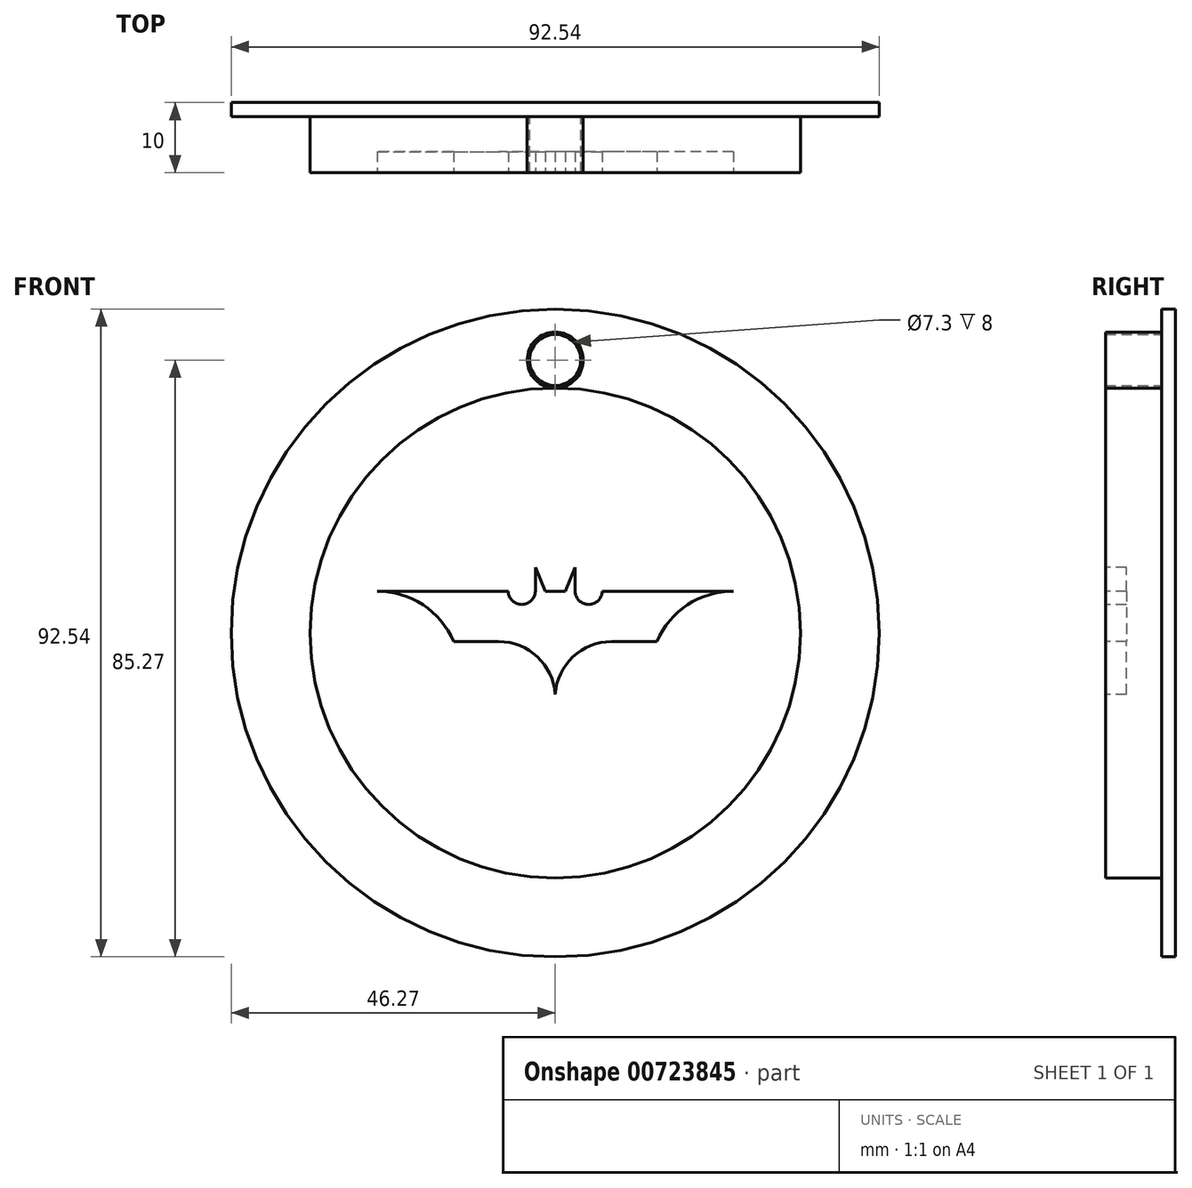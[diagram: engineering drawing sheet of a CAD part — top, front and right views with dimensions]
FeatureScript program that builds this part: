
annotation { "Feature Type Name" : "Feature", "Feature Type Description" : "" }
export const myFeature = defineFeature(function(context is Context, id is Id, definition is map)
    precondition{}
    {
        {
            var Q0;
            Q0=qCreatedBy(makeId("Front.planeOp"),FACE);
            var sketch = newSketch(context, id + "F0", { "sketchPlane" : qUnion([Q0])});
            skCircle(sketch, "E0", {"center": v(0, 0) * mm, "radius": 35 * mm});
            skLineSegment(sketch, "E1", {"start": v(0, 0) * mm, "end": v(0, 39) * mm});
            skCircle(sketch, "E2", {"center": v(0, 39) * mm, "radius": 4 * mm});
            skCircle(sketch, "E3", {"center": v(0, 39) * mm, "radius": 3.65 * mm});
            skSolve(sketch);
        }
        {
            var Q0;
            Q0 = qSketchRegion(id + "F0", true);
            extrude(context, id + "F1", {"entities" : qUnion([Q0]), "depth" : 8 * mm, "offsetDistance" : 25 * mm});
        }
        {
            var Q0;
            Q0=makeQuery(id+"F1.opExtrude","CAP_FACE",FACE,{"disambiguationData":[OSD([sQuery(id+"F0.wireOp",EDGE,"E0")])],"isStart":false});
            var sketch = newSketch(context, id + "F2", { "sketchPlane" : qUnion([Q0])});
            skArc(sketch, "E4", {"start": v(-14.5, -1.22) * mm, "mid": v(-18.9, 4.01) * mm, "end": v(-25.44, 5.97) * mm});
            skArc(sketch, "E5.MirrorCS", {"start": v(14.5, -1.22) * mm, "mid": v(18.9, 4.01) * mm, "end": v(25.44, 5.97) * mm});
            skLineSegment(sketch, "E6", {"start": v(-14.5, -1.22) * mm, "end": v(-8.07, -1.22) * mm});
            skLineSegment(sketch, "E7.MirrorCS", {"start": v(14.5, -1.22) * mm, "end": v(8.07, -1.22) * mm});
            skArc(sketch, "E8", {"start": v(0, -8.77) * mm, "mid": v(-2.54, -3.4) * mm, "end": v(-8.07, -1.22) * mm});
            skArc(sketch, "E9.MirrorCS", {"start": v(0, -8.77) * mm, "mid": v(2.54, -3.4) * mm, "end": v(8.07, -1.22) * mm});
            skLineSegment(sketch, "E10", {"start": v(-25.44, 5.97) * mm, "end": v(-6.72, 5.97) * mm});
            skArc(sketch, "E11", {"start": v(-6.72, 5.97) * mm, "mid": v(-4.78, 4.08) * mm, "end": v(-2.83, 5.97) * mm});
            skLineSegment(sketch, "E12", {"start": v(-2.83, 5.97) * mm, "end": v(-2.83, 9.36) * mm});
            skLineSegment(sketch, "E13", {"start": v(-2.83, 9.36) * mm, "end": v(-1.42, 5.97) * mm});
            skLineSegment(sketch, "E14", {"start": v(-1.42, 5.97) * mm, "end": v(0, 5.97) * mm});
            skLineSegment(sketch, "E15.MirrorCS", {"start": v(1.42, 5.97) * mm, "end": v(0, 5.97) * mm});
            skLineSegment(sketch, "E16.MirrorCS", {"start": v(2.83, 9.36) * mm, "end": v(1.42, 5.97) * mm});
            skLineSegment(sketch, "E17.MirrorCS", {"start": v(2.83, 5.97) * mm, "end": v(2.83, 9.36) * mm});
            skArc(sketch, "E18.MirrorCS", {"start": v(6.72, 5.97) * mm, "mid": v(4.78, 4.08) * mm, "end": v(2.83, 5.97) * mm});
            skLineSegment(sketch, "E19.MirrorCS", {"start": v(25.44, 5.97) * mm, "end": v(6.72, 5.97) * mm});
            skSolve(sketch);
        }
        {
            var Q0;
            Q0 = qSketchRegion(id + "F2", true);
            extrude(context, id + "F3", {"entities" : qUnion([Q0]), "operationType" : NewBodyOperationType.REMOVE, "oppositeDirection" : true, "depth" : 3 * mm, "offsetDistance" : 25 * mm});
        }
        {
            var Q0;
            Q0=qCreatedBy(makeId("Front.planeOp"),FACE);
            var sketch = newSketch(context, id + "F4", { "sketchPlane" : qUnion([Q0])});
            skCircle(sketch, "E20", {"center": v(0, 0) * mm, "radius": 46.27 * mm});
            skSolve(sketch);
        }
        {
            var Q0;
            Q0=makeQuery(id+"F4.imprint","IMPRINT",FACE,{"disambiguationData":[TD([[makeQuery(id+"F4.imprint","IMPRINT",EDGE,{"derivedFrom":sQuery(id+"F4.wireOp",EDGE,"E20")}),1.0]])]});
            extrude(context, id + "F5", {"entities" : qUnion([Q0]), "oppositeDirection" : true, "depth" : 2 * mm, "offsetDistance" : 25 * mm});
        }
    });
